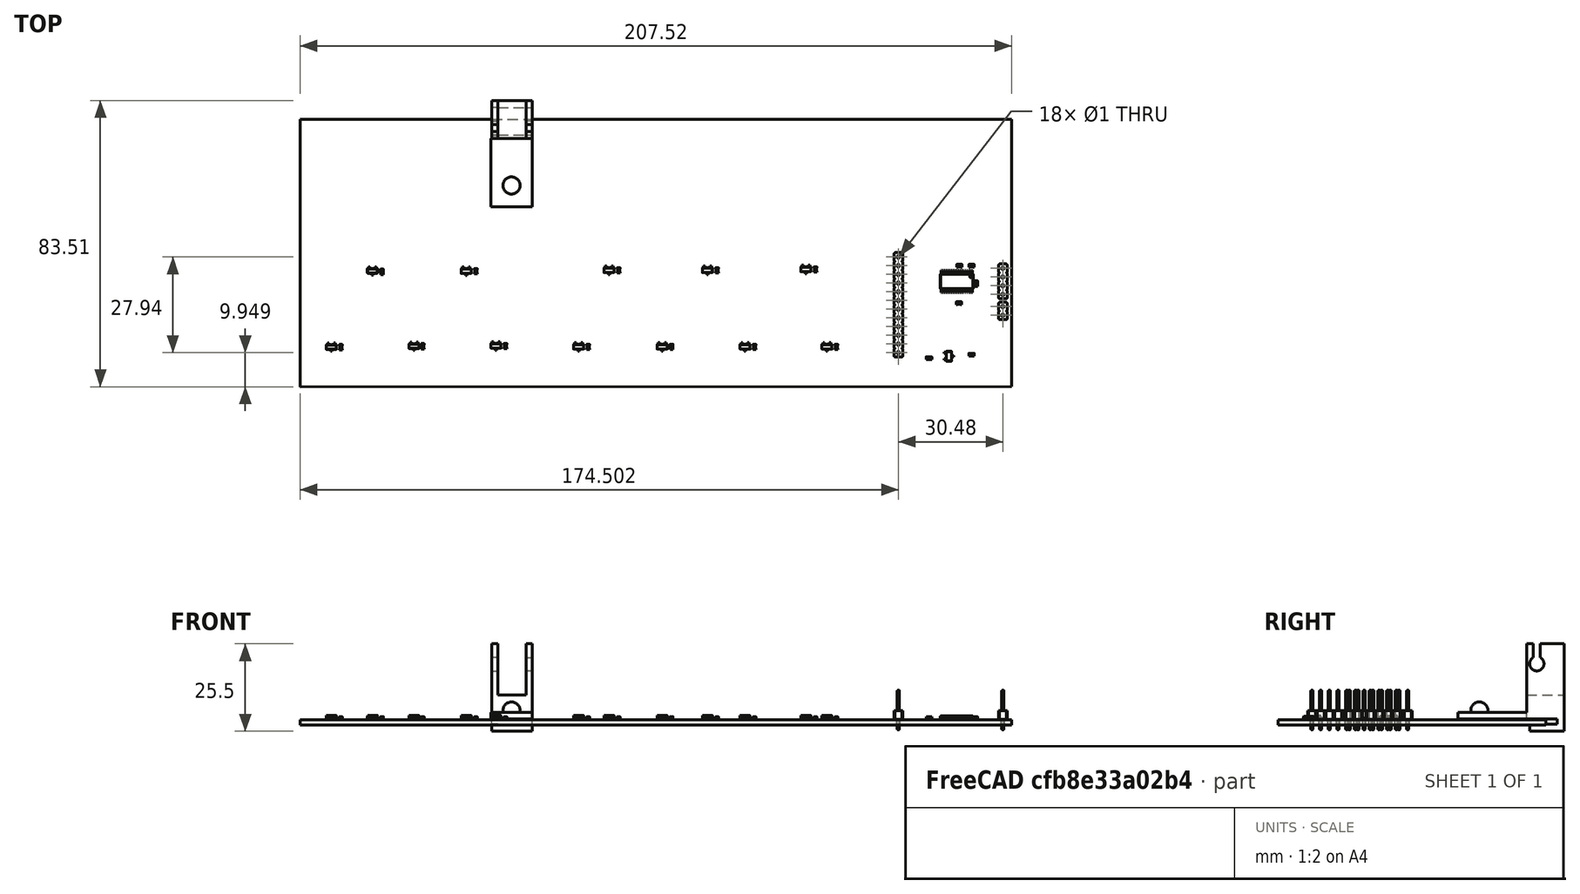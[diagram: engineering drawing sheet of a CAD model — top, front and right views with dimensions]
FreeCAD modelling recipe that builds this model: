
FCSTD DOCUMENT  (FreeCAD 0.20R29410 (Git))
Label: assembly
License: All rights reserved
LicenseURL: http://en.wikipedia.org/wiki/All_rights_reserved
objects: App::Link×13, Sketcher::SketchObject×6, PartDesign::Pad×6, App::DocumentObjectGroup×3, Mesh::Feature×2, PartDesign::Fillet×2, PartDesign::CoordinateSystem×1, App::FeaturePython×1, App::Part×1, Part::Feature×1, PartDesign::Plane×1, PartDesign::Body×1
note: 26 computed .brp shape members not serialized (recipe doc carries the construction recipe); baked Part::Feature solids carry a one-line shape summary decoded from their .brp
EXTERNAL_REF file=key_1.FCStd obj=Body
EXTERNAL_REF file=key_3.FCStd obj=Body
EXTERNAL_REF file=key_2.FCStd obj=Body
EXTERNAL_REF file=key_1A.FCStd obj=Body
EXTERNAL_REF file=key_black.FCStd obj=Body

FEATURE [App::DocumentObjectGroup] Parts
FEATURE [PartDesign::CoordinateSystem] LCS_Origin
  AttacherType = Attacher::AttachEngine3D
  MapMode = 2
  Support = -> [X_Axis]
FEATURE [App::FeaturePython] Variables  # WARN: FeaturePython — macro-defined, semantics opaque (R4)
  Type = App::PropertyContainer
FEATURE [App::DocumentObjectGroup] Constraints
FEATURE [App::DocumentObjectGroup] Configurations
FEATURE [App::Link] Body
  LinkedObject = -> <external key_1.FCStd>#Body
FEATURE [App::Link] Body001
  AttachmentOffset = pos=(-24,0,0) rot=(0,0,1;0rad)
  LinkPlacement = pos=(-28,3.33786e-06,0) rot=(0,0,1;0rad)
  LinkedObject = -> <external key_3.FCStd>#Body
  Placement = pos=(-28,3.33786e-06,0) rot=(0,0,1;0rad)
FEATURE [App::Link] Body002
  LinkPlacement = pos=(28.4,-1.74045e-06,3) rot=(0,1,0;3.14159rad)
  LinkedObject = -> <external key_3.FCStd>#Body
  Placement = pos=(28.4,-1.74045e-06,3) rot=(0,1,0;3.14159rad)
FEATURE [App::Link] Body003
  LinkPlacement = pos=(42.4,-5.05448e-06,0) rot=(0,0,1;0rad)
  LinkedObject = -> <external key_2.FCStd>#Body
  Placement = pos=(42.4,-5.05448e-06,0) rot=(0,0,1;0rad)
FEATURE [App::Link] Body005
  LinkPlacement = pos=(125.2,-7.36713e-06,3) rot=(0,1,0;3.14159rad)
  LinkedObject = -> <external key_2.FCStd>#Body
  Placement = pos=(125.2,-7.36713e-06,3) rot=(0,1,0;3.14159rad)
FEATURE [App::Link] Body008
  LinkPlacement = pos=(98.2,-1.03474e-05,3) rot=(0,1,0;3.14159rad)
  LinkedObject = -> <external key_1A.FCStd>#Body
  Placement = pos=(98.2,-1.03474e-05,3) rot=(0,1,0;3.14159rad)
FEATURE [App::Link] Body007001  label="Body007"
  LinkPlacement = pos=(69.4,-8.27312e-06,0) rot=(0,0,1;0rad)
  LinkedObject = -> <external key_1A.FCStd>#Body
  Placement = pos=(69.4,-8.27312e-06,0) rot=(0,0,1;0rad)
FEATURE [App::Link] Body007002
  LinkPlacement = pos=(-13.6,1.62125e-06,0) rot=(0,0,1;0rad)
  LinkedObject = -> <external key_black.FCStd>#Body
  Placement = pos=(-13.6,1.62125e-06,0) rot=(0,0,1;0rad)
FEATURE [App::Link] Body007003
  LinkPlacement = pos=(14,-1.66893e-06,0) rot=(0,0,1;0rad)
  LinkedObject = -> <external key_black.FCStd>#Body
  Placement = pos=(14,-1.66893e-06,0) rot=(0,0,1;0rad)
FEATURE [App::Link] Body007004
  LinkPlacement = pos=(55.5,-6.61612e-06,0) rot=(0,0,1;0rad)
  LinkedObject = -> <external key_black.FCStd>#Body
  Placement = pos=(55.5,-6.61612e-06,0) rot=(0,0,1;0rad)
FEATURE [App::Link] Body007005
  LinkPlacement = pos=(112.2,-1.33753e-05,0) rot=(0,0,1;0rad)
  LinkedObject = -> <external key_black.FCStd>#Body
  Placement = pos=(112.2,-1.33753e-05,0) rot=(0,0,1;0rad)
FEATURE [App::Link] Body007006
  LinkPlacement = pos=(84,-1.00136e-05,0) rot=(0,0,1;0rad)
  LinkedObject = -> <external key_black.FCStd>#Body
  Placement = pos=(84,-1.00136e-05,0) rot=(0,0,1;0rad)
FEATURE [App::Link] Body007007
  LinkPlacement = pos=(36,40,-15) rot=(0,0,-1;1.5708rad)
  Placement = pos=(36,40,-15) rot=(0,0,-1;1.5708rad)
FEATURE [App::Part] Assembly
  AssemblyType = Part::Link
  Group = -> [LCS_Origin,Variables,Constraints,Configurations,Body,Body001,Body002,Body003,Body005,Body007002,Body007003,Body007004,Body007005,Body007006,Body007007]
  Origin = -> Origin
  Type = Assembly
FEATURE [Mesh::Feature] key_mount_Body  label="key_mount-Body"
  Placement = pos=(-6,41,-15) rot=(0,0,1;4.71239rad)
FEATURE [Mesh::Feature] key_mount_Body001  label="key_mount-Body001"
  Placement = pos=(6,41,-15) rot=(0,0,1;4.71239rad)
FEATURE [Part::Feature] Feature  label="developmentboard"
  Placement = pos=(-88,90,-16) rot=(0,0,1;0rad)
  shape: bbox 207.5 x 78.1 x 11.54 mm, 2569 faces, 36 solids (baked)
FEATURE [Sketcher::SketchObject] Sketch002
  FullyConstrained = true
  MapMode = 5
  Placement = pos=(0,2,0) rot=(1,0,0;1.5708rad)
  sketch-geometry (13):
    g0: LineSegment StartX=7.25 StartY=0 StartZ=0 EndX=7.25 EndY=22 EndZ=0
    g1: LineSegment StartX=-3.75 StartY=22 StartZ=0 EndX=-3.75 EndY=0 EndZ=0
    g2: LineSegment StartX=-3.75 StartY=0 StartZ=0 EndX=-3.75 EndY=-3.5 EndZ=0
    g3: LineSegment StartX=-3.75 StartY=-3.5 StartZ=0 EndX=6.25 EndY=-3.5 EndZ=0
    g4: LineSegment StartX=6.25 StartY=-3.5 StartZ=0 EndX=6.25 EndY=-1.5 EndZ=0
    g5: LineSegment StartX=6.25 StartY=-1.5 StartZ=0 EndX=-1.75 EndY=-1.5 EndZ=0
    g6: LineSegment StartX=-1.75 StartY=-1.5 StartZ=0 EndX=-1.75 EndY=0 EndZ=0
    g7: LineSegment StartX=-1.75 StartY=0 StartZ=0 EndX=7.25 EndY=0 EndZ=0
    g8: ArcOfCircle CenterX=4.25 CenterY=16.1534 CenterZ=0 NormalX=0 NormalY=0 NormalZ=1 AngleXU=0 Radius=2.1 StartAngle=2.06711 EndAngle=7.35766
    g9: LineSegment StartX=5.25 StartY=18 StartZ=0 EndX=5.25 EndY=22 EndZ=0
    g10: LineSegment StartX=5.25 StartY=22 StartZ=0 EndX=7.25 EndY=22 EndZ=0
    g11: LineSegment StartX=-3.75 StartY=22 StartZ=0 EndX=3.25 EndY=22 EndZ=0
    g12: LineSegment StartX=3.25 StartY=22 StartZ=0 EndX=3.25 EndY=18 EndZ=0
  constraints (40):
    c: Vertical(g0)
    c: PointOnObject(g1,g-1)
    c: Vertical(g1)
    c: DistanceY(g0,g0) = 22
    c: DistanceY(g1,g1) = 22
    c: DistanceX(g1,g0) = 11
    c: DistanceX(g1) = -3.75
    c: Coincident(g1,g2)
    c: Vertical(g2)
    c: Coincident(g2,g3)
    c: Horizontal(g3)
    c: Coincident(g3,g4)
    c: Vertical(g4)
    c: Coincident(g4,g5)
    c: Horizontal(g5)
    c: Coincident(g5,g6)
    c: PointOnObject(g6,g-1)
    c: Vertical(g6)
    c: Coincident(g6,g7)
    c: Coincident(g7,g0)
    c: Horizontal(g7)
    c: DistanceY(g6,g6) = 1.5
    c: DistanceY(g4,g4) = 2
    c: DistanceX(g5,g-1) = 1.75
    c: DistanceX(g3,g3) = 10
    c: Radius(g8) = 2.1
    c: Horizontal(g8,g8)
    c: DistanceX(g8,g8) = 2
    c: DistanceX(g8,g0) = 2
    c: DistanceY(g8,g0) = 4
    c: Vertical(g9)
    c: Coincident(g9,g10)
    c: Coincident(g10,g0)
    c: Horizontal(g10)
    c: Coincident(g1,g11)
    c: Horizontal(g11)
    c: Coincident(g11,g12)
    c: Coincident(g12,g8)
    c: Vertical(g12)
    c: Coincident(g9,g8)
FEATURE [PartDesign::Pad] Pad
  Direction = (0,-1,2e-16)
  Length = 1.75
  Length2 = 10
  Placement = pos=(0,2,0) rot=(1,0,0;1.5708rad)
  Profile = -> Sketch002
  ReferenceAxis = -> Sketch002 [N_Axis]
  Type = 0
FEATURE [Sketcher::SketchObject] Sketch
  FullyConstrained = true
  MapMode = 5
  Placement = pos=(0,2,0) rot=(-1,0,0;1.5708rad)
  Support = -> [Pad]
  sketch-geometry (4):
    g0: LineSegment StartX=-3.75 StartY=0 StartZ=0 EndX=7.25 EndY=0 EndZ=0
    g1: LineSegment StartX=7.25 StartY=0 StartZ=0 EndX=7.25 EndY=-7 EndZ=0
    g2: LineSegment StartX=7.25 StartY=-7 StartZ=0 EndX=-3.75 EndY=-7 EndZ=0
    g3: LineSegment StartX=-3.75 StartY=-7 StartZ=0 EndX=-3.75 EndY=0 EndZ=0
  constraints (12):
    c: Coincident(g0,g1)
    c: Coincident(g1,g2)
    c: Coincident(g2,g3)
    c: Coincident(g3,g0)
    c: Horizontal(g0)
    c: Horizontal(g2)
    c: Vertical(g1)
    c: Vertical(g3)
    c: PointOnObject(g0,g-1)
    c: DistanceX(g0,g0) = 11
    c: DistanceY(g1,g1) = 7
    c: DistanceX(g-1,g0) = 7.25
FEATURE [PartDesign::Pad] Pad001
  BaseFeature = -> Pad
  Direction = (0,1,-2e-16)
  Length = 10.5
  Length2 = 10
  Placement = pos=(0,2,0) rot=(1,0,0;1.5708rad)
  Profile = -> Sketch
  ReferenceAxis = -> Sketch [N_Axis]
  Type = 0
FEATURE [PartDesign::Plane] DatumPlane
  Length = 62.4725
  MapMode = 5
  Placement = pos=(0,12.5,-2.3e-15) rot=(-1,0,0;1.5708rad)
  ResizeMode = 0
  Support = -> [Pad001]
  Width = 60.2225
FEATURE [Sketcher::SketchObject] CopySketch003
  AttachmentOffset = pos=(0,0,0) rot=(-1,0,0;3.14159rad)
  FullyConstrained = true
  MapMode = 5
  Placement = pos=(0,12.5,-2.3e-15) rot=(-1,0,0;4.71239rad)
  Support = -> [DatumPlane]
  sketch-geometry (13):
    g0: LineSegment StartX=7.25 StartY=0 StartZ=0 EndX=7.25 EndY=22 EndZ=0
    g1: LineSegment StartX=-3.75 StartY=22 StartZ=0 EndX=-3.75 EndY=0 EndZ=0
    g2: LineSegment StartX=-3.75 StartY=0 StartZ=0 EndX=-3.75 EndY=-3.5 EndZ=0
    g3: LineSegment StartX=-3.75 StartY=-3.5 StartZ=0 EndX=6.25 EndY=-3.5 EndZ=0
    g4: LineSegment StartX=6.25 StartY=-3.5 StartZ=0 EndX=6.25 EndY=-1.5 EndZ=0
    g5: LineSegment StartX=6.25 StartY=-1.5 StartZ=0 EndX=-1.75 EndY=-1.5 EndZ=0
    g6: LineSegment StartX=-1.75 StartY=-1.5 StartZ=0 EndX=-1.75 EndY=0 EndZ=0
    g7: LineSegment StartX=-1.75 StartY=0 StartZ=0 EndX=7.25 EndY=0 EndZ=0
    g8: ArcOfCircle CenterX=4.25 CenterY=16.1534 CenterZ=0 NormalX=0 NormalY=0 NormalZ=1 AngleXU=0 Radius=2.1 StartAngle=2.06711 EndAngle=7.35766
    g9: LineSegment StartX=5.25 StartY=18 StartZ=0 EndX=5.25 EndY=22 EndZ=0
    g10: LineSegment StartX=5.25 StartY=22 StartZ=0 EndX=7.25 EndY=22 EndZ=0
    g11: LineSegment StartX=-3.75 StartY=22 StartZ=0 EndX=3.25 EndY=22 EndZ=0
    g12: LineSegment StartX=3.25 StartY=22 StartZ=0 EndX=3.25 EndY=18 EndZ=0
  constraints (40):
    c: Vertical(g0)
    c: PointOnObject(g1,g-1)
    c: Vertical(g1)
    c: DistanceY(g0,g0) = 22
    c: DistanceY(g1,g1) = 22
    c: DistanceX(g1,g0) = 11
    c: DistanceX(g1) = -3.75
    c: Coincident(g1,g2)
    c: Vertical(g2)
    c: Coincident(g2,g3)
    c: Horizontal(g3)
    c: Coincident(g3,g4)
    c: Vertical(g4)
    c: Coincident(g4,g5)
    c: Horizontal(g5)
    c: Coincident(g5,g6)
    c: PointOnObject(g6,g-1)
    c: Vertical(g6)
    c: Coincident(g6,g7)
    c: Coincident(g7,g0)
    c: Horizontal(g7)
    c: DistanceY(g6,g6) = 1.5
    c: DistanceY(g4,g4) = 2
    c: DistanceX(g5,g-1) = 1.75
    c: DistanceX(g3,g3) = 10
    c: Radius(g8) = 2.1
    c: Horizontal(g8,g8)
    c: DistanceX(g8,g8) = 2
    c: DistanceX(g8,g0) = 2
    c: DistanceY(g8,g0) = 4
    c: Vertical(g9)
    c: Coincident(g9,g10)
    c: Coincident(g10,g0)
    c: Horizontal(g10)
    c: Coincident(g1,g11)
    c: Horizontal(g11)
    c: Coincident(g11,g12)
    c: Coincident(g12,g8)
    c: Vertical(g12)
    c: Coincident(g9,g8)
FEATURE [PartDesign::Pad] Pad002
  BaseFeature = -> Pad001
  Direction = (0,1,-3e-16)
  Length = 1.75
  Length2 = 10
  Placement = pos=(0,2,0) rot=(1,0,0;1.5708rad)
  Profile = -> CopySketch003
  ReferenceAxis = -> Pad001 [Edge38]
  Type = 0
FEATURE [Sketcher::SketchObject] Sketch003
  FullyConstrained = true
  MapMode = 5
  Placement = pos=(7.25,2,0) rot=(0.707107,0,0.707107;3.14159rad)
  Support = -> [Pad002]
  sketch-geometry (4):
    g0: LineSegment StartX=0 StartY=1.75 StartZ=0 EndX=2 EndY=1.75 EndZ=0
    g1: LineSegment StartX=2 StartY=1.75 StartZ=0 EndX=2 EndY=-12.25 EndZ=0
    g2: LineSegment StartX=2 StartY=-12.25 StartZ=0 EndX=0 EndY=-12.25 EndZ=0
    g3: LineSegment StartX=0 StartY=-12.25 StartZ=0 EndX=0 EndY=1.75 EndZ=0
  constraints (12):
    c: Coincident(g0,g1)
    c: Coincident(g1,g2)
    c: Coincident(g2,g3)
    c: Coincident(g3,g0)
    c: Horizontal(g0)
    c: Horizontal(g2)
    c: Vertical(g1)
    c: Vertical(g3)
    c: PointOnObject(g0,g-2)
    c: DistanceY(g1,g1) = 14
    c: DistanceY(g-1,g0) = 1.75
    c: DistanceX(g0,g0) = 2
FEATURE [PartDesign::Pad] Pad003
  BaseFeature = -> Pad002
  Direction = (1,0,-2e-16)
  Length = 20
  Length2 = 10
  Placement = pos=(0,2,0) rot=(1,0,0;1.5708rad)
  Profile = -> Sketch003
  ReferenceAxis = -> Sketch003 [N_Axis]
  Type = 0
FEATURE [Sketcher::SketchObject] Sketch004
  FullyConstrained = true
  MapMode = 5
  Placement = pos=(4e-16,2,2) rot=(0,0,1;3.14159rad)
  Support = -> [Pad003]
  sketch-geometry (1):
    g0: Circle CenterX=-21 CenterY=-5 CenterZ=0 NormalX=0 NormalY=0 NormalZ=1 AngleXU=0 Radius=2.5
  constraints (3):
    c: Diameter(g0) = 5
    c: DistanceY(g0,g-1) = 5
    c: DistanceX(g0,g-1) = 21
FEATURE [PartDesign::Pad] Pad004
  BaseFeature = -> Pad003
  Direction = (2e-16,3e-16,1)
  Length = 3
  Length2 = 10
  Placement = pos=(0,2,0) rot=(1,0,0;1.5708rad)
  Profile = -> Sketch004
  ReferenceAxis = -> Sketch004 [N_Axis]
  Type = 0
FEATURE [PartDesign::Fillet] Fillet
  Base = -> Pad004 [Edge106]
  BaseFeature = -> Pad004
  Placement = pos=(0,2,0) rot=(1,0,0;1.5708rad)
  Radius = 2.5
  SupportTransform = false
  UseAllEdges = false
FEATURE [PartDesign::Fillet] Fillet002
  Base = -> Pad004 [Edge103]
  BaseFeature = -> Pad004
  Placement = pos=(0,2,0) rot=(1,0,0;1.5708rad)
  Radius = 2
  SupportTransform = false
  UseAllEdges = false
FEATURE [Sketcher::SketchObject] Sketch008
  FullyConstrained = true
  MapMode = 5
  Placement = pos=(0,2,0) rot=(-1,0,0;1.5708rad)
  Support = -> [Fillet]
  sketch-geometry (6):
    g0: LineSegment StartX=-3.75 StartY=0 StartZ=0 EndX=-3.75 EndY=3.5 EndZ=0
    g1: LineSegment StartX=-3.75 StartY=3.5 StartZ=0 EndX=6.25 EndY=3.5 EndZ=0
    g2: LineSegment StartX=6.25 StartY=3.5 StartZ=0 EndX=6.25 EndY=1.5 EndZ=0
    g3: LineSegment StartX=6.25 StartY=1.5 StartZ=0 EndX=-1.75 EndY=1.5 EndZ=0
    g4: LineSegment StartX=-1.75 StartY=1.5 StartZ=0 EndX=-1.75 EndY=0 EndZ=0
    g5: LineSegment StartX=-1.75 StartY=0 StartZ=0 EndX=-3.75 EndY=0 EndZ=0
  constraints (18):
    c: Vertical(g0)
    c: Coincident(g0,g1)
    c: Horizontal(g1)
    c: Coincident(g1,g2)
    c: Vertical(g2)
    c: Coincident(g2,g3)
    c: Horizontal(g3)
    c: Coincident(g3,g4)
    c: Vertical(g4)
    c: Coincident(g4,g5)
    c: Coincident(g5,g0)
    c: Horizontal(g5)
    c: DistanceX(g1,g1) = 10
    c: DistanceY(g0,g0) = 3.5
    c: DistanceY(g2,g2) = 2
    c: DistanceY(g4,g-1) = 0
    c: DistanceX(g5,g5) = 2
    c: DistanceX(g4,g-1) = 1.75
FEATURE [PartDesign::Pad] Pad008
  BaseFeature = -> Fillet
  Direction = (0,1,-7e-16)
  Length = 10
  Length2 = 10
  Placement = pos=(0,2,0) rot=(1,0,0;1.5708rad)
  Profile = -> Sketch008
  ReferenceAxis = -> Sketch008 [N_Axis]
  Type = 0
FEATURE [PartDesign::Body] Body007008
  Group = -> [Sketch002,Pad,Sketch,Pad001,CopySketch003,Pad002,Sketch003,Pad003,Sketch004,Pad004,DatumPlane,Fillet,Sketch008,Pad008,Fillet002]
  Origin = -> Origin001
  Placement = pos=(21.25,44.5,-14.25) rot=(0,0,1;4.71239rad)
  Tip = -> Fillet002

RESOLVED EXTERNAL PARTS (link-assembly join: the EXTERNAL_REF files above that resolve inside this repo's crawl, each included once):
---- part key_1.FCStd = doc fcstd_f6e496b9c629 ----
FCSTD DOCUMENT  (FreeCAD 0.20R29177 (Git))
Label: key_1
License: All rights reserved
LicenseURL: http://en.wikipedia.org/wiki/All_rights_reserved
objects: Sketcher::SketchObject×4, PartDesign::Pad×3, PartDesign::Pocket×1, App::MeasureDistance×1, PartDesign::Fillet×1, PartDesign::Body×1
note: 15 computed .brp shape members not serialized (recipe doc carries the construction recipe); baked Part::Feature solids carry a one-line shape summary decoded from their .brp

FEATURE [Sketcher::SketchObject] Sketch
  FullyConstrained = true
  MapMode = 5
  Support = -> [XY_Plane]
  sketch-geometry (13):
    g0: LineSegment StartX=-11.75 StartY=-33 StartZ=0 EndX=11.75 EndY=-33 EndZ=0
    g1: LineSegment StartX=11.75 StartY=-33 StartZ=0 EndX=11.75 EndY=-11.5 EndZ=0
    g2: LineSegment StartX=11.75 StartY=-11.5 StartZ=0 EndX=7 EndY=-11.5 EndZ=0
    g3: LineSegment StartX=7 StartY=-11.5 StartZ=0 EndX=7 EndY=33 EndZ=0
    g4: LineSegment StartX=7 StartY=33 StartZ=0 EndX=4 EndY=33 EndZ=0
    g5: LineSegment StartX=4 StartY=33 StartZ=0 EndX=4 EndY=43 EndZ=0
    g6: LineSegment StartX=4 StartY=43 StartZ=0 EndX=-4 EndY=43 EndZ=0
    g7: LineSegment StartX=-4 StartY=43 StartZ=0 EndX=-4 EndY=33 EndZ=0
    g8: LineSegment StartX=-4 StartY=33 StartZ=0 EndX=-7 EndY=33 EndZ=0
    g9: LineSegment StartX=-4 StartY=33 StartZ=0 EndX=4 EndY=33 EndZ=0
    g10: LineSegment StartX=-11.75 StartY=-33 StartZ=0 EndX=-11.75 EndY=-11.5 EndZ=0
    g11: LineSegment StartX=-11.75 StartY=-11.5 StartZ=0 EndX=-7 EndY=-11.5 EndZ=0
    g12: LineSegment StartX=-7 StartY=-11.5 StartZ=0 EndX=-7 EndY=33 EndZ=0
  constraints (38):
    c: Horizontal(g0)
    c: Coincident(g0,g1)
    c: Vertical(g1)
    c: Coincident(g1,g2)
    c: Coincident(g2,g3)
    c: Vertical(g3)
    c: Coincident(g3,g4)
    c: Coincident(g4,g5)
    c: Coincident(g5,g6)
    c: Coincident(g6,g7)
    c: Coincident(g7,g8)
    c: Horizontal(g8)
    c: Horizontal(g4)
    c: Horizontal(g6)
    c: Vertical(g7)
    c: Vertical(g5)
    c: Horizontal(g2)
    c: DistanceX(g0,g0) = 23.5
    c: DistanceX(g8,g3) = 14
    c: DistanceX(g8,g8) = 3
    c: DistanceY(g5,g5) = 10
    c: Coincident(g9,g7)
    c: Coincident(g9,g4)
    c: Horizontal(g9)
    c: DistanceY(g0,g8) = 66
    c: DistanceY(g1,g1) = 21.5
    c: DistanceY(g0,g-1) = 33
    c: DistanceX(g7,g-1) = 4
    c: Coincident(g0,g10)
    c: Vertical(g10)
    c: Coincident(g10,g11)
    c: Coincident(g11,g12)
    c: Coincident(g12,g8)
    c: Vertical(g12)
    c: DistanceY(g10,g10) = 21.5
    c: Horizontal(g11)
    c: Equal(g11,g2)
    c: DistanceX(g6,g6) = 8
FEATURE [PartDesign::Pad] Pad
  Direction = (0,0,1)
  Length = 3
  Length2 = 100
  Profile = -> Sketch
  Type = 0
FEATURE [Sketcher::SketchObject] Sketch001
  FullyConstrained = true
  MapMode = 5
  Placement = pos=(0,0,0) rot=(0.57735,0.57735,0.57735;2.0944rad)
  Support = -> [YZ_Plane]
  sketch-geometry (1):
    g0: Circle CenterX=40 CenterY=1.5 CenterZ=0 NormalX=0 NormalY=0 NormalZ=1 AngleXU=0 Radius=1.5
  constraints (3):
    c: Tangent(g0,g-1)
    c: Radius(g0) = 1.5
    c: DistanceX(g-1,g0) = 40
FEATURE [PartDesign::Pad] Pad001
  BaseFeature = -> Pad
  Direction = (1,-2e-16,3e-16)
  Length = 12
  Length2 = 100
  Midplane = true
  Profile = -> Sketch001
  Type = 0
FEATURE [Sketcher::SketchObject] Sketch002
  FullyConstrained = true
  MapMode = 5
  Placement = pos=(0,0,3) rot=(0,0,1;0rad)
  Support = -> [Pad001]
  sketch-geometry (1):
    g0: Circle CenterX=0 CenterY=-23 CenterZ=0 NormalX=0 NormalY=0 NormalZ=1 AngleXU=0 Radius=2.1
  constraints (3):
    c: Diameter(g0) = 4.2
    c: DistanceX(g0,g-1) = 0
    c: DistanceY(g0,g-1) = 23
FEATURE [PartDesign::Pocket] Pocket
  BaseFeature = -> Pad001
  Direction = (0,0,-1)
  Length = 2
  Length2 = 5
  Profile = -> Sketch002
  ReferenceAxis = -> Sketch002 [N_Axis]
  Type = 0
FEATURE [Sketcher::SketchObject] Sketch003
  FullyConstrained = true
  MapMode = 5
  Placement = pos=(0,0,3) rot=(0,0,1;0rad)
  Support = -> [Pocket]
  sketch-geometry (1):
    g0: Circle CenterX=0 CenterY=23 CenterZ=0 NormalX=0 NormalY=0 NormalZ=1 AngleXU=0 Radius=3
  constraints (3):
    c: PointOnObject(g0,g-2)
    c: Diameter(g0) = 6
    c: DistanceY(g-1,g0) = 23
FEATURE [App::MeasureDistance] Distance  label="Distance: 19.80 mm"
  Distance = 19.7998
  P1 = (3.08621,22.7854,3)
  P2 = (3.16036,42.585,3)
FEATURE [PartDesign::Pad] Pad002
  BaseFeature = -> Pocket
  Direction = (0,0,1)
  Length = 3
  Length2 = 10
  Profile = -> Sketch003
  ReferenceAxis = -> Sketch003 [N_Axis]
  Type = 0
FEATURE [PartDesign::Fillet] Fillet
  Base = -> Pad002 [Edge48]
  BaseFeature = -> Pad002
  Radius = 2.5
  SupportTransform = false
  UseAllEdges = false
FEATURE [PartDesign::Body] Body  label="key_1"
  Group = -> [Sketch,Pad,Sketch001,Pad001,Sketch002,Pocket,Sketch003,Pad002,Fillet]
  Origin = -> Origin
  Tip = -> Fillet
---- part key_1A.FCStd = doc fcstd_954d1c3bc9bb ----
FCSTD DOCUMENT  (FreeCAD 0.19R24415 (Git))
Label: key_1A
License: All rights reserved
LicenseURL: http://en.wikipedia.org/wiki/All_rights_reserved
objects: Sketcher::SketchObject×2, PartDesign::Pad×2, PartDesign::Body×1
note: 7 computed .brp shape members not serialized (recipe doc carries the construction recipe); baked Part::Feature solids carry a one-line shape summary decoded from their .brp

FEATURE [Sketcher::SketchObject] Sketch
  FullyConstrained = false
  MapMode = 5
  Support = -> [XY_Plane]
  sketch-geometry (13):
    g0: LineSegment StartX=-9.25 StartY=-33 StartZ=0 EndX=14.25 EndY=-33 EndZ=0
    g1: LineSegment StartX=14.25 StartY=-33 StartZ=0 EndX=14.25 EndY=-11.5 EndZ=0
    g2: LineSegment StartX=14.25 StartY=-11.5 StartZ=0 EndX=7 EndY=-11.5 EndZ=0
    g3: LineSegment StartX=7 StartY=-11.5 StartZ=0 EndX=7 EndY=33 EndZ=0
    g4: LineSegment StartX=7 StartY=33 StartZ=0 EndX=4 EndY=33 EndZ=0
    g5: LineSegment StartX=4 StartY=33 StartZ=0 EndX=4 EndY=43 EndZ=0
    g6: LineSegment StartX=4 StartY=43 StartZ=0 EndX=-4 EndY=43 EndZ=0
    g7: LineSegment StartX=-4 StartY=43 StartZ=0 EndX=-4 EndY=33 EndZ=0
    g8: LineSegment StartX=-4 StartY=33 StartZ=0 EndX=-7 EndY=33 EndZ=0
    g9: LineSegment StartX=-4 StartY=33 StartZ=0 EndX=4 EndY=33 EndZ=0
    g10: LineSegment StartX=-9.25 StartY=-33 StartZ=0 EndX=-9.25 EndY=-11.5 EndZ=0
    g11: LineSegment StartX=-9.25 StartY=-11.5 StartZ=0 EndX=-7 EndY=-11.5 EndZ=0
    g12: LineSegment StartX=-7 StartY=-11.5 StartZ=0 EndX=-7 EndY=33 EndZ=0
  constraints (37):
    c: Horizontal(g0)
    c: Coincident(g0,g1)
    c: Vertical(g1)
    c: Coincident(g1,g2)
    c: Coincident(g2,g3)
    c: Vertical(g3)
    c: Coincident(g3,g4)
    c: Coincident(g4,g5)
    c: Coincident(g5,g6)
    c: Coincident(g6,g7)
    c: Coincident(g7,g8)
    c: Horizontal(g8)
    c: Horizontal(g4)
    c: Horizontal(g6)
    c: Vertical(g7)
    c: Vertical(g5)
    c: Horizontal(g2)
    c: DistanceX(g0,g0) = 23.5
    c: DistanceX(g8,g3) = 14
    c: DistanceX(g8,g8) = 3
    c: DistanceY(g5,g5) = 10
    c: Coincident(g9,g7)
    c: Coincident(g9,g4)
    c: Horizontal(g9)
    c: DistanceY(g0,g8) = 66
    c: DistanceY(g1,g1) = 21.5
    c: DistanceY(g0,g-1) = 33
    c: DistanceX(g7,g-1) = 4
    c: Coincident(g0,g10)
    c: Vertical(g10)
    c: Coincident(g10,g11)
    c: Coincident(g11,g12)
    c: Coincident(g12,g8)
    c: Vertical(g12)
    c: DistanceY(g10,g10) = 21.5
    c: DistanceX(g6,g6) = 8
    c: DistanceX(g11,g11) = 2.25
FEATURE [PartDesign::Pad] Pad
  Direction = (1,1,1)
  Length = 3
  Length2 = 100
  Profile = -> Sketch
  Type = 0
FEATURE [Sketcher::SketchObject] Sketch001
  FullyConstrained = true
  MapMode = 5
  Placement = pos=(0,0,0) rot=(0.57735,0.57735,0.57735;2.0944rad)
  Support = -> [YZ_Plane]
  sketch-geometry (1):
    g0: Circle CenterX=40 CenterY=1.5 CenterZ=0 NormalX=0 NormalY=0 NormalZ=1 AngleXU=0 Radius=1.5
  constraints (3):
    c: Tangent(g0,g-1)
    c: Radius(g0) = 1.5
    c: DistanceX(g-1,g0) = 40
FEATURE [PartDesign::Pad] Pad001
  BaseFeature = -> Pad
  Direction = (1,1,1)
  Length = 12
  Length2 = 100
  Midplane = true
  Profile = -> Sketch001
  Type = 0
FEATURE [PartDesign::Body] Body  label="key_1a"
  Group = -> [Sketch,Pad,Sketch001,Pad001]
  Origin = -> Origin
  Tip = -> Pad001
---- part key_2.FCStd = doc fcstd_9ed31f56f3b8 ----
FCSTD DOCUMENT  (FreeCAD 0.20R29410 (Git))
Label: key_2
License: All rights reserved
LicenseURL: http://en.wikipedia.org/wiki/All_rights_reserved
objects: Sketcher::SketchObject×2, PartDesign::Pad×2, PartDesign::Body×1, App::MeasureDistance×1
note: 7 computed .brp shape members not serialized (recipe doc carries the construction recipe); baked Part::Feature solids carry a one-line shape summary decoded from their .brp

FEATURE [Sketcher::SketchObject] Sketch
  FullyConstrained = true
  MapMode = 5
  Support = -> [XY_Plane]
  sketch-geometry (11):
    g0: LineSegment StartX=-6.25 StartY=33 StartZ=0 EndX=-6.25 EndY=-33 EndZ=0
    g1: LineSegment StartX=-6.25 StartY=-33 StartZ=0 EndX=17.25 EndY=-33 EndZ=0
    g2: LineSegment StartX=17.25 StartY=-33 StartZ=0 EndX=17.25 EndY=-11.5 EndZ=0
    g3: LineSegment StartX=17.25 StartY=-11.5 StartZ=0 EndX=6.25 EndY=-11.5 EndZ=0
    g4: LineSegment StartX=6.25 StartY=-11.5 StartZ=0 EndX=6.25 EndY=33 EndZ=0
    g5: LineSegment StartX=6.25 StartY=33 StartZ=0 EndX=4 EndY=33 EndZ=0
    g6: LineSegment StartX=4 StartY=33 StartZ=0 EndX=4 EndY=43 EndZ=0
    g7: LineSegment StartX=4 StartY=43 StartZ=0 EndX=-4 EndY=43 EndZ=0
    g8: LineSegment StartX=-4 StartY=43 StartZ=0 EndX=-4 EndY=33 EndZ=0
    g9: LineSegment StartX=-4 StartY=33 StartZ=0 EndX=-6.25 EndY=33 EndZ=0
    g10: LineSegment StartX=-4 StartY=33 StartZ=0 EndX=4 EndY=33 EndZ=0
  constraints (32):
    c: Vertical(g0)
    c: Coincident(g0,g1)
    c: Horizontal(g1)
    c: Coincident(g1,g2)
    c: Vertical(g2)
    c: Coincident(g2,g3)
    c: Coincident(g3,g4)
    c: Vertical(g4)
    c: Coincident(g4,g5)
    c: Coincident(g5,g6)
    c: Coincident(g6,g7)
    c: Coincident(g7,g8)
    c: Coincident(g8,g9)
    c: Coincident(g9,g0)
    c: Horizontal(g9)
    c: Horizontal(g5)
    c: Horizontal(g7)
    c: Vertical(g8)
    c: Vertical(g6)
    c: Horizontal(g3)
    c: DistanceX(g1,g1) = 23.5
    c: DistanceX(g0,g4) = 12.5
    c: DistanceX(g7,g7) = 8
    c: DistanceX(g9,g9) = 2.25
    c: DistanceY(g6,g6) = 10
    c: Coincident(g10,g8)
    c: Coincident(g10,g5)
    c: Horizontal(g10)
    c: DistanceY(g0,g0) = 66
    c: DistanceY(g2,g2) = 21.5
    c: DistanceY(g0,g-1) = 33
    c: DistanceX(g8,g-1) = 4
FEATURE [PartDesign::Pad] Pad
  Direction = (1,1,1)
  Length = 3
  Length2 = 100
  Profile = -> Sketch
  Type = 0
FEATURE [Sketcher::SketchObject] Sketch001
  FullyConstrained = true
  MapMode = 5
  Placement = pos=(0,0,0) rot=(0.57735,0.57735,0.57735;2.0944rad)
  Support = -> [YZ_Plane]
  sketch-geometry (1):
    g0: Circle CenterX=40 CenterY=1.5 CenterZ=0 NormalX=0 NormalY=0 NormalZ=1 AngleXU=0 Radius=1.5
  constraints (3):
    c: Tangent(g0,g-1)
    c: Radius(g0) = 1.5
    c: DistanceX(g-1,g0) = 40
FEATURE [PartDesign::Pad] Pad001
  BaseFeature = -> Pad
  Direction = (1,1,1)
  Length = 12
  Length2 = 100
  Midplane = true
  Profile = -> Sketch001
  Type = 0
FEATURE [PartDesign::Body] Body  label="key_2"
  Group = -> [Sketch,Pad,Sketch001,Pad001]
  Origin = -> Origin
  Tip = -> Pad001
FEATURE [App::MeasureDistance] Distance  label="Distance: 8.00 mm"
  Distance = 8
  P1 = (-4,43,3)
  P2 = (4,43,3)
---- part key_3.FCStd = doc fcstd_5bb0a050483e ----
FCSTD DOCUMENT  (FreeCAD 0.20R29177 (Git))
Label: key_3
License: All rights reserved
LicenseURL: http://en.wikipedia.org/wiki/All_rights_reserved
objects: Sketcher::SketchObject×3, PartDesign::Pad×2, PartDesign::Pocket×1, PartDesign::Body×1
note: 10 computed .brp shape members not serialized (recipe doc carries the construction recipe); baked Part::Feature solids carry a one-line shape summary decoded from their .brp

FEATURE [Sketcher::SketchObject] Sketch
  FullyConstrained = true
  MapMode = 5
  Support = -> [XY_Plane]
  sketch-geometry (11):
    g0: LineSegment StartX=-7.75 StartY=33 StartZ=0 EndX=-7.75 EndY=-33 EndZ=0
    g1: LineSegment StartX=-7.75 StartY=-33 StartZ=0 EndX=15.75 EndY=-33 EndZ=0
    g2: LineSegment StartX=15.75 StartY=-33 StartZ=0 EndX=15.75 EndY=-11.5 EndZ=0
    g3: LineSegment StartX=15.75 StartY=-11.5 StartZ=0 EndX=7.75 EndY=-11.5 EndZ=0
    g4: LineSegment StartX=7.75 StartY=-11.5 StartZ=0 EndX=7.75 EndY=33 EndZ=0
    g5: LineSegment StartX=7.75 StartY=33 StartZ=0 EndX=5 EndY=33 EndZ=0
    g6: LineSegment StartX=5 StartY=33 StartZ=0 EndX=5 EndY=43 EndZ=0
    g7: LineSegment StartX=5 StartY=43 StartZ=0 EndX=-5 EndY=43 EndZ=0
    g8: LineSegment StartX=-5 StartY=43 StartZ=0 EndX=-5 EndY=33 EndZ=0
    g9: LineSegment StartX=-5 StartY=33 StartZ=0 EndX=-7.75 EndY=33 EndZ=0
    g10: LineSegment StartX=-5 StartY=33 StartZ=0 EndX=5 EndY=33 EndZ=0
  constraints (32):
    c: Vertical(g0)
    c: Coincident(g0,g1)
    c: Horizontal(g1)
    c: Coincident(g1,g2)
    c: Vertical(g2)
    c: Coincident(g2,g3)
    c: Coincident(g3,g4)
    c: Vertical(g4)
    c: Coincident(g4,g5)
    c: Coincident(g5,g6)
    c: Coincident(g6,g7)
    c: Coincident(g7,g8)
    c: Coincident(g8,g9)
    c: Coincident(g9,g0)
    c: Horizontal(g9)
    c: Horizontal(g5)
    c: Horizontal(g7)
    c: Vertical(g8)
    c: Vertical(g6)
    c: Horizontal(g3)
    c: DistanceX(g1,g1) = 23.5
    c: DistanceX(g0,g4) = 15.5
    c: DistanceX(g7,g7) = 10
    c: DistanceX(g9,g9) = 2.75
    c: DistanceY(g6,g6) = 10
    c: Coincident(g10,g8)
    c: Coincident(g10,g5)
    c: Horizontal(g10)
    c: DistanceY(g0,g0) = 66
    c: DistanceY(g2,g2) = 21.5
    c: DistanceY(g0,g-1) = 33
    c: DistanceX(g8,g-1) = 5
FEATURE [PartDesign::Pad] Pad
  Direction = (0,0,1)
  Length = 3
  Length2 = 100
  Profile = -> Sketch
  Type = 0
FEATURE [Sketcher::SketchObject] Sketch001
  FullyConstrained = true
  MapMode = 5
  Placement = pos=(0,0,0) rot=(0.57735,0.57735,0.57735;2.0944rad)
  Support = -> [YZ_Plane]
  sketch-geometry (1):
    g0: Circle CenterX=40 CenterY=1.5 CenterZ=0 NormalX=0 NormalY=0 NormalZ=1 AngleXU=0 Radius=1.5
  constraints (3):
    c: Tangent(g0,g-1)
    c: Radius(g0) = 1.5
    c: DistanceX(g-1,g0) = 40
FEATURE [PartDesign::Pad] Pad001
  BaseFeature = -> Pad
  Direction = (1,-2e-16,3e-16)
  Length = 14.5
  Length2 = 100
  Midplane = true
  Profile = -> Sketch001
  Type = 0
FEATURE [Sketcher::SketchObject] Sketch002
  FullyConstrained = true
  MapMode = 5
  Placement = pos=(0,0,3) rot=(0,0,1;0rad)
  Support = -> [Pad001]
  sketch-geometry (5):
    g0: LineSegment StartX=15.75 StartY=-11.5 StartZ=0 EndX=15.75 EndY=-33 EndZ=0
    g1: LineSegment StartX=15.75 StartY=-33 StartZ=0 EndX=-7.75 EndY=-33 EndZ=0
    g2: LineSegment StartX=-7.75 StartY=-33 StartZ=0 EndX=-7.75 EndY=-11.5 EndZ=0
    g3: LineSegment StartX=-7.75 StartY=-11.5 StartZ=0 EndX=15.75 EndY=-11.5 EndZ=0
    g4: Circle CenterX=4 CenterY=-23 CenterZ=0 NormalX=0 NormalY=0 NormalZ=1 AngleXU=0 Radius=2.1
  constraints (15):
    c: Vertical(g0)
    c: Coincident(g0,g1)
    c: Horizontal(g1)
    c: Coincident(g1,g2)
    c: Vertical(g2)
    c: Coincident(g2,g3)
    c: Coincident(g3,g0)
    c: Horizontal(g3)
    c: DistanceX(g1,g1) = 23.5
    c: DistanceY(g0,g0) = 21.5
    c: DistanceY(g1,g-1) = 33
    c: DistanceX(g2,g-1) = 7.75
    c: DistanceY(g0,g4) = 10
    c: DistanceX(g4,g0) = 11.75
    c: Diameter(g4) = 4.2
FEATURE [PartDesign::Pocket] Pocket
  BaseFeature = -> Pad001
  Direction = (0,0,-1)
  Length = 2
  Length2 = 5
  Profile = -> Sketch002
  ReferenceAxis = -> Sketch002 [N_Axis]
  Type = 0
FEATURE [PartDesign::Body] Body  label="key_3"
  Group = -> [Sketch,Pad,Sketch001,Pad001,Sketch002,Pocket]
  Origin = -> Origin
  Tip = -> Pocket
---- part key_black.FCStd = doc fcstd_35b2309e0150 ----
FCSTD DOCUMENT  (FreeCAD 0.20R29410 (Git))
Label: key_black
License: All rights reserved
LicenseURL: http://en.wikipedia.org/wiki/All_rights_reserved
objects: Sketcher::SketchObject×4, PartDesign::Pad×3, PartDesign::Pocket×1, PartDesign::Fillet×1, App::MeasureDistance×1, PartDesign::Chamfer×1, PartDesign::Body×1
note: 17 computed .brp shape members not serialized (recipe doc carries the construction recipe); baked Part::Feature solids carry a one-line shape summary decoded from their .brp

FEATURE [Sketcher::SketchObject] Sketch
  FullyConstrained = true
  MapMode = 5
  Support = -> [XY_Plane]
  sketch-geometry (9):
    g0: LineSegment StartX=6.5 StartY=-11 StartZ=0 EndX=6.5 EndY=33 EndZ=0
    g1: LineSegment StartX=6.5 StartY=33 StartZ=0 EndX=5 EndY=33 EndZ=0
    g2: LineSegment StartX=5 StartY=33 StartZ=0 EndX=5 EndY=43 EndZ=0
    g3: LineSegment StartX=5 StartY=43 StartZ=0 EndX=-5 EndY=43 EndZ=0
    g4: LineSegment StartX=-5 StartY=43 StartZ=0 EndX=-5 EndY=33 EndZ=0
    g5: LineSegment StartX=-5 StartY=33 StartZ=0 EndX=-6.5 EndY=33 EndZ=0
    g6: LineSegment StartX=-5 StartY=33 StartZ=0 EndX=5 EndY=33 EndZ=0
    g7: LineSegment StartX=-6.5 StartY=-11 StartZ=0 EndX=-6.5 EndY=33 EndZ=0
    g8: LineSegment StartX=6.5 StartY=-11 StartZ=0 EndX=-6.5 EndY=-11 EndZ=0
  constraints (26):
    c: Vertical(g0)
    c: Coincident(g0,g1)
    c: Coincident(g1,g2)
    c: Coincident(g2,g3)
    c: Coincident(g3,g4)
    c: Coincident(g4,g5)
    c: Horizontal(g5)
    c: Horizontal(g1)
    c: Horizontal(g3)
    c: Vertical(g4)
    c: Vertical(g2)
    c: DistanceX(g5,g0) = 13
    c: DistanceX(g5,g5) = 1.5
    c: DistanceY(g2,g2) = 10
    c: Coincident(g6,g4)
    c: Coincident(g6,g1)
    c: Horizontal(g6)
    c: DistanceX(g4,g-1) = 5
    c: Coincident(g7,g5)
    c: Vertical(g7)
    c: DistanceX(g3,g3) = 10
    c: Coincident(g8,g0)
    c: Coincident(g8,g7)
    c: Horizontal(g8)
    c: DistanceY(g0,g0) = 44
    c: DistanceY(g-1,g5) = 33
FEATURE [PartDesign::Pad] Pad
  Direction = (0,0,1)
  Length = 9
  Length2 = 100
  Profile = -> Sketch
  Type = 0
FEATURE [Sketcher::SketchObject] Sketch001
  FullyConstrained = true
  MapMode = 5
  Placement = pos=(0,0,0) rot=(0.57735,0.57735,0.57735;2.0944rad)
  Support = -> [YZ_Plane]
  sketch-geometry (1):
    g0: Circle CenterX=40 CenterY=1.5 CenterZ=0 NormalX=0 NormalY=0 NormalZ=1 AngleXU=0 Radius=1.5
  constraints (3):
    c: Tangent(g0,g-1)
    c: Radius(g0) = 1.5
    c: DistanceX(g-1,g0) = 40
FEATURE [PartDesign::Pad] Pad001
  BaseFeature = -> Pad
  Direction = (1,-2e-16,3e-16)
  Length = 14
  Length2 = 100
  Midplane = true
  Profile = -> Sketch001
  Type = 0
FEATURE [Sketcher::SketchObject] Sketch002
  FullyConstrained = true
  MapMode = 5
  Placement = pos=(0,0,0) rot=(1,0,0;3.14159rad)
  Support = -> [Pad001]
  sketch-geometry (2):
    g0: LineSegment StartX=-6.5 StartY=11 StartZ=0 EndX=6.5 EndY=11 EndZ=0
    g1: Circle CenterX=0 CenterY=1 CenterZ=0 NormalX=0 NormalY=0 NormalZ=1 AngleXU=0 Radius=2
  constraints (7):
    c: Horizontal(g0)
    c: DistanceX(g0,g0) = 13
    c: DistanceY(g-1,g0) = 11
    c: DistanceX(g0,g-1) = 6.5
    c: PointOnObject(g1,g-2)
    c: DistanceY(g1,g0) = 10
    c: Diameter(g1) = 4
FEATURE [PartDesign::Pocket] Pocket
  BaseFeature = -> Pad001
  Direction = (0,0,1)
  Length = 2
  Length2 = 5
  Profile = -> Sketch002
  ReferenceAxis = -> Sketch002 [N_Axis]
  Type = 0
FEATURE [Sketcher::SketchObject] Sketch003
  FullyConstrained = true
  MapMode = 5
  Placement = pos=(0,0,0) rot=(1,0,0;3.14159rad)
  Support = -> [Pocket]
  sketch-geometry (2):
    g0: LineSegment StartX=-5 StartY=-43 StartZ=0 EndX=5 EndY=-43 EndZ=0
    g1: Circle CenterX=0 CenterY=-23 CenterZ=0 NormalX=0 NormalY=0 NormalZ=1 AngleXU=0 Radius=3
  constraints (7):
    c: Horizontal(g0)
    c: DistanceX(g0,g0) = 10
    c: DistanceX(g0,g-1) = 5
    c: DistanceY(g0,g-1) = 43
    c: PointOnObject(g1,g-2)
    c: Diameter(g1) = 6
    c: DistanceY(g0,g1) = 20
FEATURE [PartDesign::Pad] Pad002
  BaseFeature = -> Pocket
  Direction = (0,0,-1)
  Length = 3
  Length2 = 10
  Profile = -> Sketch003
  ReferenceAxis = -> Sketch003 [N_Axis]
  Type = 0
FEATURE [PartDesign::Fillet] Fillet
  Base = -> Pad002 [Edge37]
  BaseFeature = -> Pad002
  Radius = 2.75
  SupportTransform = false
  UseAllEdges = false
FEATURE [App::MeasureDistance] Distance  label="Distance: 43.88 mm"
  Distance = 43.8788
  P1 = (-2.00866,-0.874555,3.1e-15)
  P2 = (-2.62009,43,0)
FEATURE [PartDesign::Chamfer] Chamfer
  Angle = 45
  Base = -> Fillet [Edge17]
  BaseFeature = -> Fillet
  ChamferType = 0
  FlipDirection = false
  Size = 8
  Size2 = 1
  SupportTransform = false
  UseAllEdges = false
FEATURE [PartDesign::Body] Body  label="key_black"
  Group = -> [Sketch,Pad,Sketch001,Pad001,Sketch002,Pocket,Sketch003,Pad002,Fillet,Chamfer]
  Origin = -> Origin
  Tip = -> Chamfer
